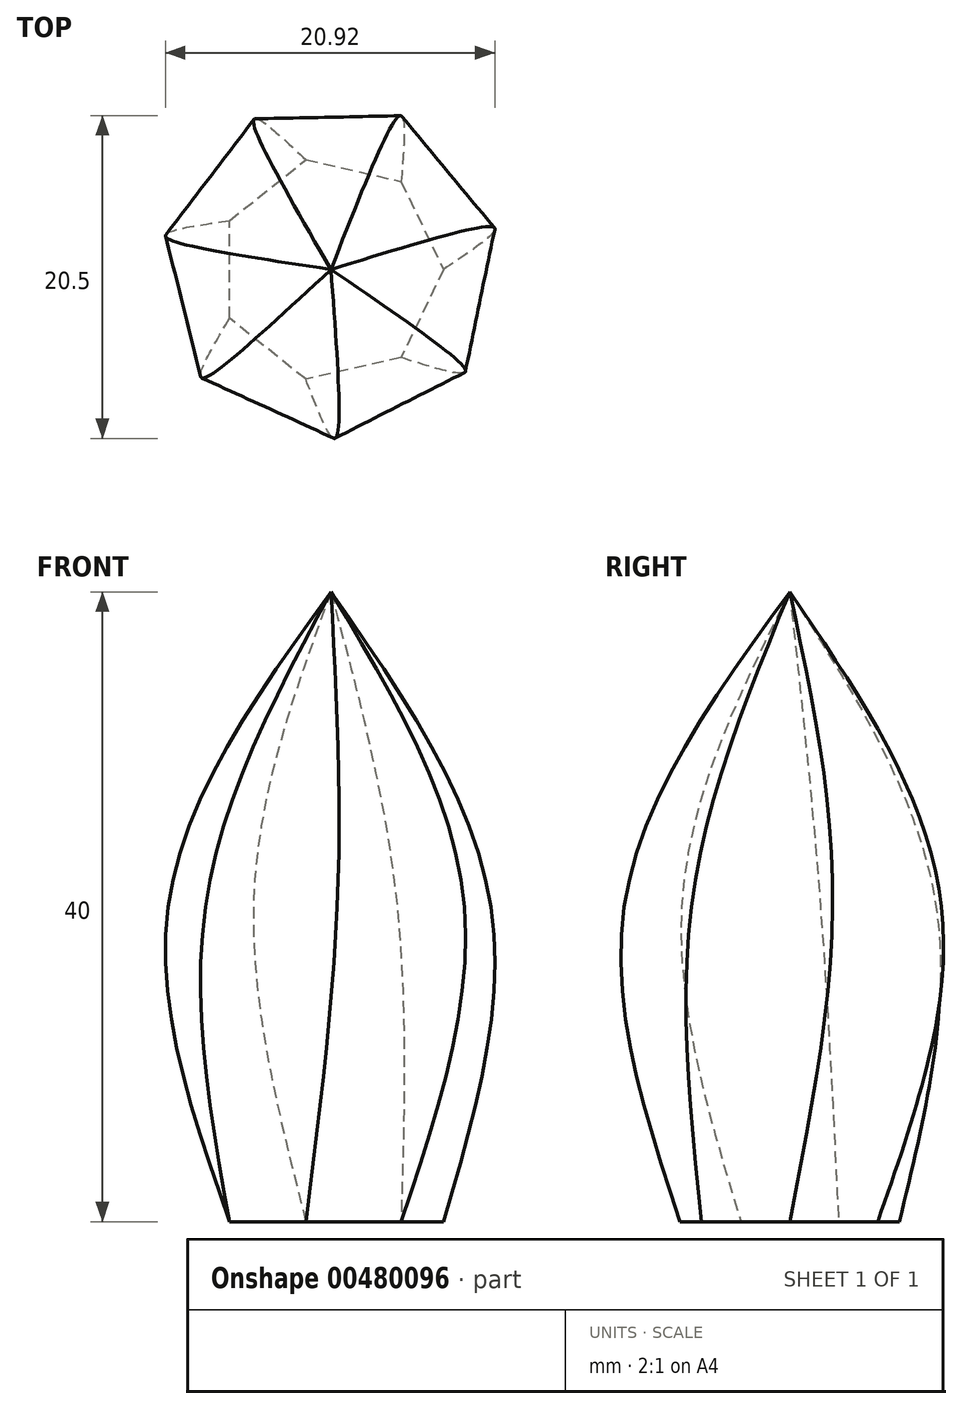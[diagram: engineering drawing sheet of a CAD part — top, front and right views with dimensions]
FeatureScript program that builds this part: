
annotation { "Feature Type Name" : "Feature", "Feature Type Description" : "" }
export const myFeature = defineFeature(function(context is Context, id is Id, definition is map)
    precondition{}
    {
        {
            var Q0;
            Q0=qCreatedBy(makeId("Top.planeOp"),FACE);
            var sketch = newSketch(context, id + "F0", { "sketchPlane" : qUnion([Q0])});
            skCircle(sketch, "E0.cCircle", {"center": v(0, 0) * mm, "radius": 7.15 * mm, "construction": true});
            skLineSegment(sketch, "E0.0", {"start": v(7.15, 0) * mm, "end": v(4.46, -5.6) * mm});
            skLineSegment(sketch, "E0.1", {"start": v(4.46, -5.6) * mm, "end": v(-1.6, -6.97) * mm});
            skLineSegment(sketch, "E0.2", {"start": v(-1.6, -6.97) * mm, "end": v(-6.44, -3.1) * mm});
            skLineSegment(sketch, "E0.3", {"start": v(-6.44, -3.1) * mm, "end": v(-6.44, 3.1) * mm});
            skLineSegment(sketch, "E0.4", {"start": v(-6.44, 3.1) * mm, "end": v(-1.6, 6.97) * mm});
            skLineSegment(sketch, "E0.5", {"start": v(-1.6, 6.97) * mm, "end": v(4.46, 5.6) * mm});
            skLineSegment(sketch, "E0.6", {"start": v(4.46, 5.6) * mm, "end": v(7.15, 0) * mm});
            skSolve(sketch);
        }
        {
            var Q0;
            Q0=qCreatedBy(makeId("Top.planeOp"),FACE);
            cPlane(context, id + "F1", {"entities" : qUnion([Q0]), "cplaneType" : CPlaneType.OFFSET, "offset" : 10 * mm, "width" : 150 * mm, "height" : 150 * mm});
        }
        {
            var Q0;
            Q0=qCreatedBy(id+"F1.planeOp",FACE);
            cPlane(context, id + "F2", {"entities" : qUnion([Q0]), "cplaneType" : CPlaneType.OFFSET, "offset" : 10 * mm, "width" : 150 * mm, "height" : 150 * mm});
        }
        {
            var Q0;
            Q0=qCreatedBy(id+"F2.planeOp",FACE);
            var sketch = newSketch(context, id + "F3", { "sketchPlane" : qUnion([Q0])});
            skCircle(sketch, "E1.cCircle", {"center": v(0, 0) * mm, "radius": 10.52 * mm, "construction": true});
            skLineSegment(sketch, "E1.0", {"start": v(10.16, 2.73) * mm, "end": v(8.47, -6.24) * mm});
            skLineSegment(sketch, "E1.1", {"start": v(8.47, -6.24) * mm, "end": v(0.4, -10.51) * mm});
            skLineSegment(sketch, "E1.2", {"start": v(0.4, -10.51) * mm, "end": v(-7.97, -6.87) * mm});
            skLineSegment(sketch, "E1.3", {"start": v(-7.97, -6.87) * mm, "end": v(-10.34, 1.95) * mm});
            skLineSegment(sketch, "E1.4", {"start": v(-10.34, 1.95) * mm, "end": v(-4.92, 9.3) * mm});
            skLineSegment(sketch, "E1.5", {"start": v(-4.92, 9.3) * mm, "end": v(4.2, 9.65) * mm});
            skLineSegment(sketch, "E1.6", {"start": v(4.2, 9.65) * mm, "end": v(10.16, 2.73) * mm});
            skSolve(sketch);
        }
        {
            var Q0;
            Q0=qCreatedBy(id+"F2.planeOp",FACE);
            cPlane(context, id + "F4", {"entities" : qUnion([Q0]), "cplaneType" : CPlaneType.OFFSET, "offset" : 20 * mm, "width" : 150 * mm, "height" : 150 * mm});
        }
        {
            var Q0;
            Q0=qCreatedBy(id+"F4.planeOp",FACE);
            var sketch = newSketch(context, id + "F5", { "sketchPlane" : qUnion([Q0])});
            skCircle(sketch, "E2", {"center": v(0, 0) * mm, "radius": 0.41 * mm});
            skSolve(sketch);
        }
        {
            var Q0;
            Q0=sQuery(id+"F5.wireOp",VERTEX,"E2.center");
            var Q1;
            Q1=makeQuery(id+"F3.imprint","IMPRINT",FACE,{"disambiguationData":[TD([[makeQuery(id+"F3.imprint","IMPRINT",EDGE,{"derivedFrom":sQuery(id+"F3.wireOp",EDGE,"E1.0")}),-1.0]])]});
            var Q2;
            Q2=makeQuery(id+"F0.imprint","IMPRINT",FACE,{"disambiguationData":[TD([[makeQuery(id+"F0.imprint","IMPRINT",EDGE,{"derivedFrom":sQuery(id+"F0.wireOp",EDGE,"E0.0")}),-1.0]])]});
            loft(context, id + "F6", {"sheetProfilesArray" : [{ "sheetProfileEntities" : qUnion([Q0]) }, { "sheetProfileEntities" : qUnion([Q1]) }, { "sheetProfileEntities" : qUnion([Q2]) }]});
        }
    });
